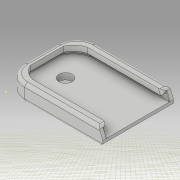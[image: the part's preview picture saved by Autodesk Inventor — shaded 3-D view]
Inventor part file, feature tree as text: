
AUTODESK INVENTOR PART (.ipt)
format: ipt  version: 2018 (Build 220112000, 112)  size: 306,176 bytes
history: native  units: in
note: dims shown in document units (in); Inventor stores cm internally (conversion verified against a paired STEP export)
features: sketch x9, extrude x6, fillet x3, mirror x2, sweep x1, plane x1, chamfer x1
ambient origin geometry x8: Origin, YZ Plane, XZ Plane, XY Plane, X Axis, Y Axis, Z Axis, Center Point
bodies: Solid1 (feature_tree)
feature tree (23):
  extrude  "Extrusion1"  Depth=1.133in
  fillet  "Fillet1"  Radius=0.1in
  extrude  "Extrusion2"  Depth=0.124in
  sweep  "Sweep1"
  plane  "Work Plane1"
  mirror  "Mirror1"
  extrude  "Extrusion3"  Depth=0.16in TaperAngle=0.0deg
  chamfer  "Chamfer1"  [1 undecoded]
  extrude  "Extrusion4"  Depth=1.0857in
  mirror  "Mirror2"
  extrude  "Extrusion5"  Depth=0.05in TaperAngle=45.0deg
  fillet  "Fillet2"  Radius=2.0in
  fillet  "Fillet3"  Radius=0.087in
  sketch  "Sketch10"  dims[d28=0.385in d29=0.18in]
  extrude  "Extrusion6"  Depth=0.18in
  sketch  "Sketch1"  dims[d0=1.548in d1=1.133in d2=0.1in d3=0.0in]
  sketch  "Sketch3"  dims[d5=0.3in d6=0.124in]
  sketch  "Sketch4"  dims[d7=0.124in d9=0.3in]
  sketch  "Sketch5"  dims[d10=0.3in d11=0.16in d12=0.0in]
  sketch  "Sketch6"  dims[d15=0.075in d16=0.0in d17=0.0in]
  sketch  "Sketch7"  dims[d18=0.1in d19=1.0857in]
  sketch  "Sketch9"  dims[d20=2.0in d21=0.0in d22=0.05in d23=0.125in d24=45.0deg d25=2.0in d26=0.0in d27=0.087in]
  sketch  "Sketch11"  dims[d30=1.0in d31=0.0in d32=0.05in d33=0.008in d50=0.21in d51=1.0in d52=0.0in]
note: 1 required parameter value undecoded (feature->parameter linkage not recoverable at this tier; creation-order binding heuristic only, values carry confidence <= 0.55)
